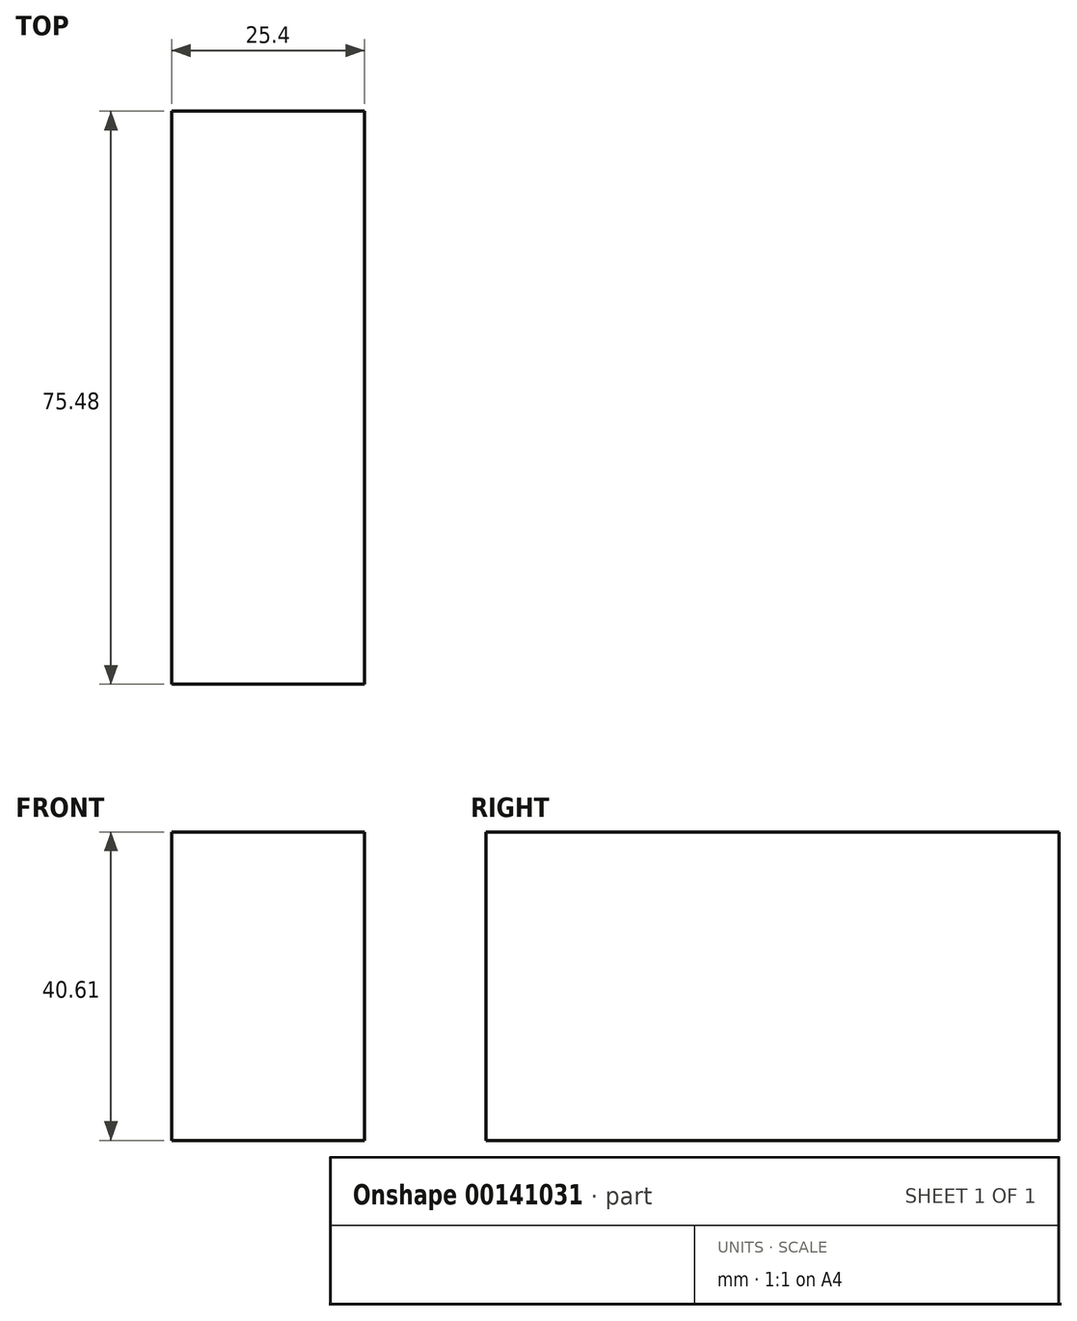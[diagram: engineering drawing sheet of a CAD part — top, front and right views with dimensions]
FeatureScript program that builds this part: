
annotation { "Feature Type Name" : "Feature", "Feature Type Description" : "" }
export const myFeature = defineFeature(function(context is Context, id is Id, definition is map)
    precondition{}
    {
        {
            var Q0;
            Q0=qCreatedBy(makeId("Right.planeOp"),FACE);
            var sketch = newSketch(context, id + "F0", { "sketchPlane" : qUnion([Q0])});
            skLineSegment(sketch, "E0.bottom", {"start": v(-39.07, 19.98) * mm, "end": v(36.41, 19.98) * mm});
            skLineSegment(sketch, "E0.top", {"start": v(-39.07, -20.63) * mm, "end": v(36.41, -20.63) * mm});
            skLineSegment(sketch, "E0.left", {"start": v(-39.07, 19.98) * mm, "end": v(-39.07, -20.63) * mm});
            skLineSegment(sketch, "E0.right", {"start": v(36.41, 19.98) * mm, "end": v(36.41, -20.63) * mm});
            skSolve(sketch);
        }
        {
            var Q0;
            Q0=makeQuery(id+"F0.imprint","IMPRINT",FACE,{"disambiguationData":[TD([[makeQuery(id+"F0.imprint","IMPRINT",EDGE,{"derivedFrom":sQuery(id+"F0.wireOp",EDGE,"E0.bottom")}),-1.0]])]});
            extrude(context, id + "F1", {"entities" : qUnion([Q0]), "depth" : 25.4 * mm});
        }
    });
